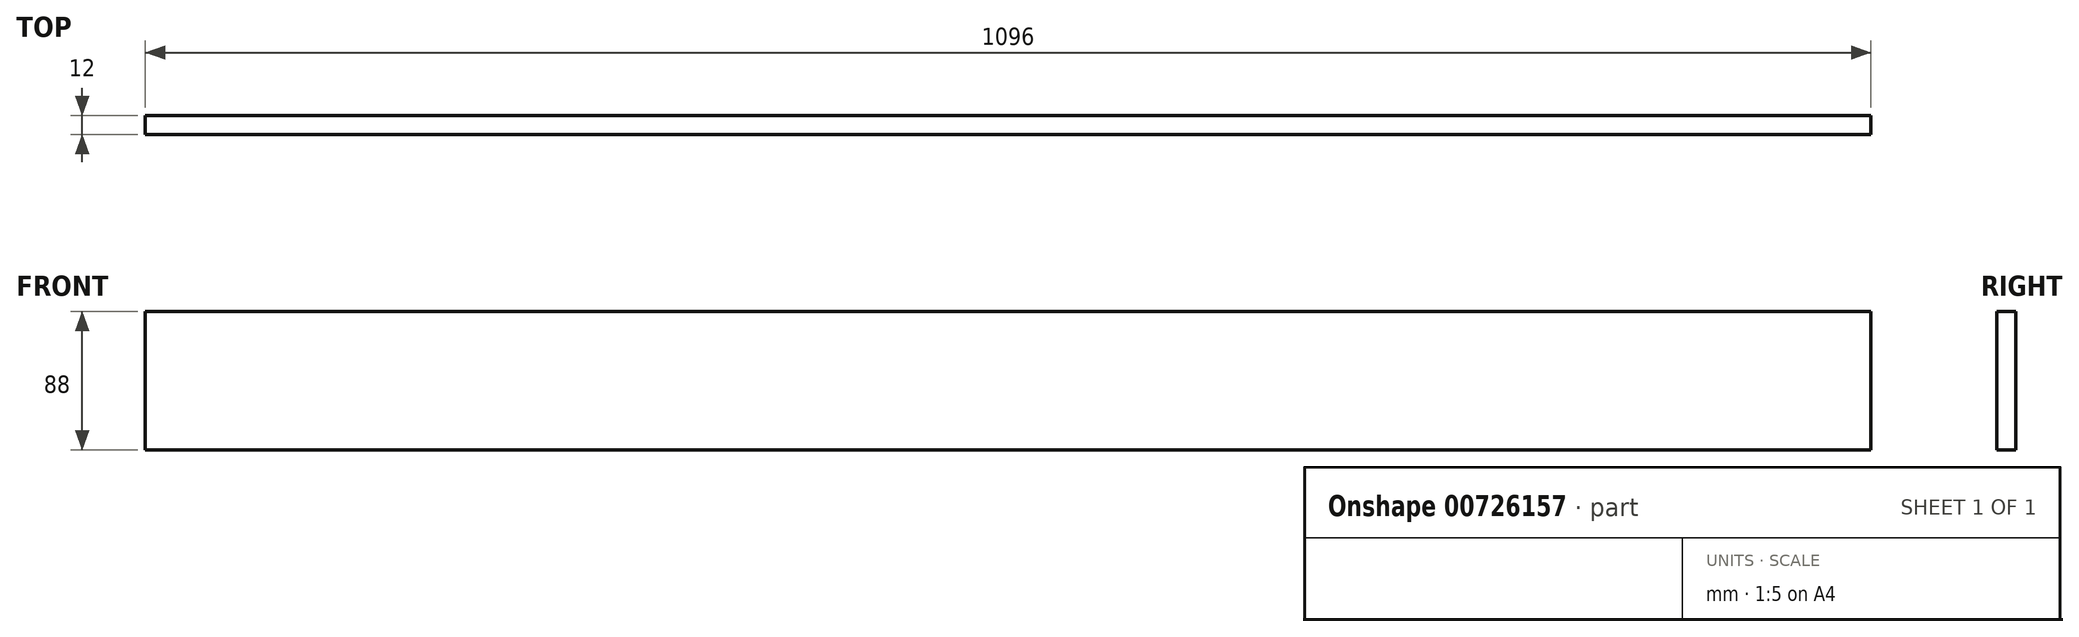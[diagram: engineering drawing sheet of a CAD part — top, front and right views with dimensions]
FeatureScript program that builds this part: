
annotation { "Feature Type Name" : "Feature", "Feature Type Description" : "" }
export const myFeature = defineFeature(function(context is Context, id is Id, definition is map)
    precondition{}
    {
        {
            var Q0;
            Q0=qCreatedBy(makeId("Front.planeOp"),FACE);
            var sketch = newSketch(context, id + "F0", { "sketchPlane" : qUnion([Q0])});
            skLineSegment(sketch, "E0.bottom", {"start": v(-548, 44) * mm, "end": v(548, 44) * mm});
            skLineSegment(sketch, "E0.top", {"start": v(-548, -44) * mm, "end": v(548, -44) * mm});
            skLineSegment(sketch, "E0.left", {"start": v(-548, 44) * mm, "end": v(-548, -44) * mm});
            skLineSegment(sketch, "E0.right", {"start": v(548, 44) * mm, "end": v(548, -44) * mm});
            skLineSegment(sketch, "E1", {"start": v(0, -44) * mm, "end": v(0, 44) * mm, "construction": true});
            skSolve(sketch);
        }
        {
            var Q0;
            Q0 = qSketchRegion(id + "F0", true);
            extrude(context, id + "F1", {"entities" : qUnion([Q0]), "depth" : 12 * mm, "offsetDistance" : 25 * mm});
        }
    });
